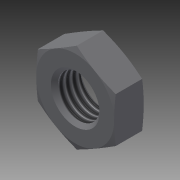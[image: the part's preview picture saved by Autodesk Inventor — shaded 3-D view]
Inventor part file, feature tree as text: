
AUTODESK INVENTOR PART (.ipt)
format: ipt  version: 2014 (Build 180170000, 170)  size: 162,816 bytes
history: native  units: in
note: dims shown in document units (in); Inventor stores cm internally (conversion verified against a paired STEP export)
features: other x70, sketch x3, revolve x2, extrude x1, thread x1
ambient origin geometry x8: Origin, YZ Plane, XZ Plane, XY Plane, X Axis, Y Axis, Z Axis, Center Point
bodies: Solid1 (feature_tree)
feature tree (77):
  sketch  "Sketch_8"  dims[d0=360.0deg d1=0.19in d2=0.0in]
  sketch  "Sketch_10"  dims[d3=360.0deg d4=0.1449in d5=0.0in]
  revolve  "Revolution1"  [1 undecoded]
  extrude  "Extrusion1"  Depth=0.1449in TaperAngle=0.0deg
  revolve  "Revolution2"  [1 undecoded]
  thread  "Thread1"  [1 undecoded]
  other  "NUT_XY"
  other  "NUT_YZ"
  other  "NUT_ZX"
  other  "NUT_X"
  other  "NUT_Y"
  other  "NUT_Z"
  other  "NUT_Center"
  other  "a1_XY"
  other  "a1_YZ"
  other  "a1_ZX"
  other  "a1_X"
  other  "a1_Y"
  other  "a1_Z"
  other  "a1_Center"
  other  "a2_XY"
  other  "a2_YZ"
  other  "a2_ZX"
  other  "a2_X"
  other  "a2_Y"
  other  "a2_Z"
  other  "a2_Center"
  other  "b1_XY"
  other  "b1_YZ"
  other  "b1_ZX"
  other  "b1_X"
  other  "b1_Y"
  other  "b1_Z"
  other  "b1_Center"
  other  "b2_XY"
  other  "b2_YZ"
  other  "b2_ZX"
  other  "b2_X"
  other  "b2_Y"
  other  "b2_Z"
  other  "b2_Center"
  other  "e_XY"
  other  "e_YZ"
  other  "e_ZX"
  other  "e_X"
  other  "e_Y"
  other  "e_Z"
  other  "e_Center"
  other  "ol1_XY"
  other  "ol1_YZ"
  other  "ol1_ZX"
  other  "ol1_X"
  other  "ol1_Y"
  other  "ol1_Z"
  other  "ol1_Center"
  other  "ol2_XY"
  other  "ol2_YZ"
  other  "ol2_ZX"
  other  "ol2_X"
  other  "ol2_Y"
  other  "ol2_Z"
  other  "ol2_Center"
  other  "th1_XY"
  other  "th1_YZ"
  other  "th1_ZX"
  other  "th1_X"
  other  "th1_Y"
  other  "th1_Z"
  other  "th1_Center"
  other  "th2_XY"
  other  "th2_YZ"
  other  "th2_ZX"
  other  "th2_X"
  other  "th2_Y"
  other  "th2_Z"
  other  "th2_Center"
  sketch  "Sketch_11"
note: 3 required parameter values undecoded (feature->parameter linkage not recoverable at this tier; creation-order binding heuristic only, values carry confidence <= 0.55)